# Revit family: P200603KR-006c_KUBR214KPA
name_source: partatom
category: Specialty Equipment
units: mm (PartAtom-declared; Revit-internal decimal feet)

## family parameters
Always vertical = Yes
Cut with Voids When Loaded = No
Enable Cutting in Views = No
Maintain Annotation Orientation = No
Part Type = Normal
Room Calculation Point = No
Round Connector Dimension = Use Diameter
Shared = No
Work Plane-Based = No

## types (2) — shared parameters
Amps = 0 A
Back Panel Material = ARCAT - Metal - Aluminum
Body Material = ARCAT - Metal - Steel - Black
Clearance Material = ARCAT - Clearance
Default Elevation = 0"
Depth = 26 1/4"
Description = Beverage Center
Display Panel Material = ARCAT - Plastic - Black
Door Material = ARCAT - Metal - Steel - Cream
Glass Material = ARCAT - Glass - Gray
Handle Material = ARCAT - Metal - Steel -Gray
Height = 34 3/8"
Leg Material = ARCAT - Plastic - Black
Manufacturer = KitchenAid
Screw Material = ARCAT - Metal - Steel - Stainless
Tray Material = ARCAT - Wooden
Voltage = 0 V
Width = 23 7/8"

## per-type parameters (varying)
| type | Left Swing | Right Swing |
| KUBR214KPA | No | Yes |
| KUBL214KPA | Yes | No |

note: column(s) folded — value = type name in every type: Model

## geometry (parser evidence)
native form markers: Sweep x2
no freeform markers — native parametric forms only
